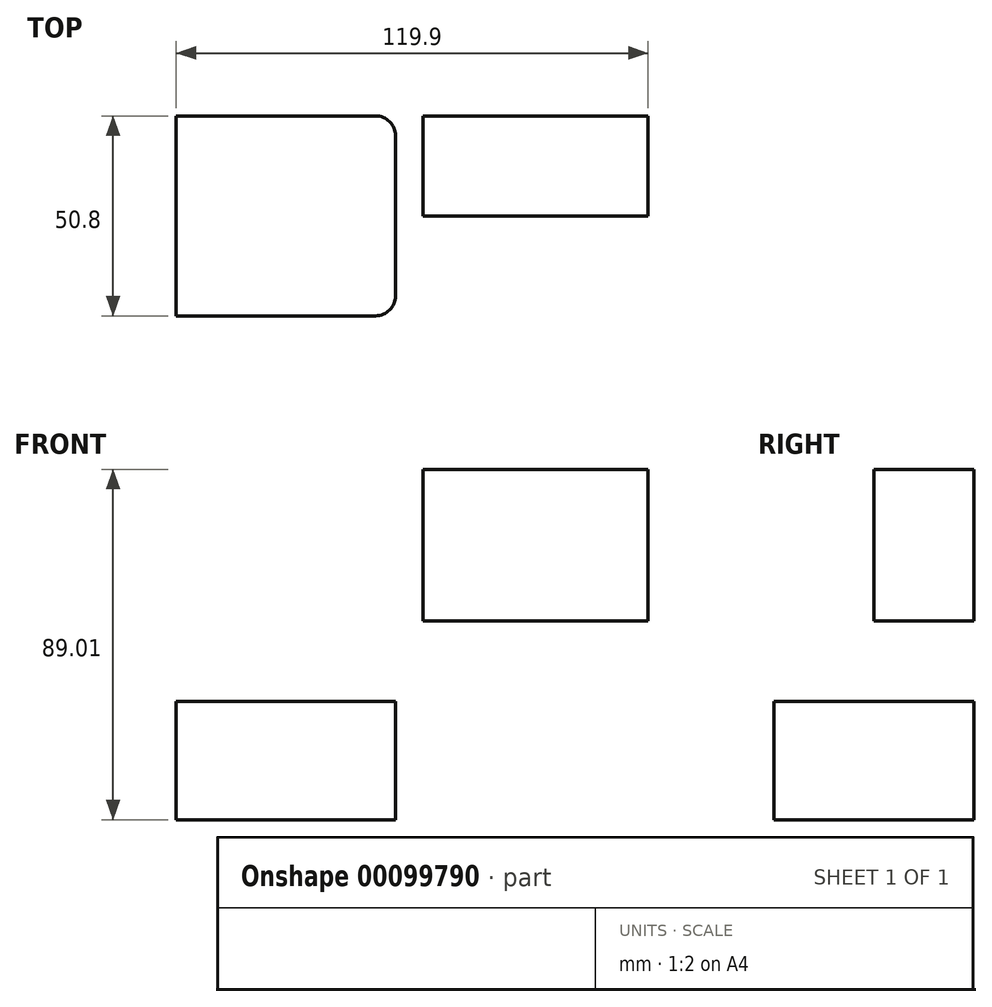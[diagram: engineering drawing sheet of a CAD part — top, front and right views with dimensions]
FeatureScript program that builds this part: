
annotation { "Feature Type Name" : "Feature", "Feature Type Description" : "" }
export const myFeature = defineFeature(function(context is Context, id is Id, definition is map)
    precondition{}
    {
        {
            var Q0;
            Q0=qCreatedBy(makeId("Front.planeOp"),FACE);
            var sketch = newSketch(context, id + "F0", { "sketchPlane" : qUnion([Q0])});
            skLineSegment(sketch, "E0.bottom", {"start": v(46.63, 19.3) * mm, "end": v(-46.63, 19.3) * mm});
            skLineSegment(sketch, "E0.top", {"start": v(46.63, -19.3) * mm, "end": v(-46.63, -19.3) * mm});
            skLineSegment(sketch, "E0.left", {"start": v(46.63, 19.3) * mm, "end": v(46.63, -19.3) * mm});
            skLineSegment(sketch, "E0.right", {"start": v(-46.63, 19.3) * mm, "end": v(-46.63, -19.3) * mm});
            skPoint(sketch, "E0.middle", {"position": v(0, 0) * mm});
            skLineSegment(sketch, "E1.bottom", {"start": v(110.8, 39.7) * mm, "end": v(53.63, 39.7) * mm});
            skLineSegment(sketch, "E1.top", {"start": v(110.8, 78.21) * mm, "end": v(53.63, 78.21) * mm});
            skLineSegment(sketch, "E1.left", {"start": v(110.8, 39.7) * mm, "end": v(110.8, 78.21) * mm});
            skLineSegment(sketch, "E1.right", {"start": v(53.63, 39.7) * mm, "end": v(53.63, 78.21) * mm});
            skPoint(sketch, "E1.middle", {"position": v(82.22, 58.96) * mm});
            skLineSegment(sketch, "E2", {"start": v(46.63, 19.3) * mm, "end": v(46.63, 45.25) * mm});
            skArc(sketch, "E3", {"start": v(46.63, 45.25) * mm, "mid": v(50.53, 53.16) * mm, "end": v(59.17, 54.88) * mm});
            skLineSegment(sketch, "E4.bottom", {"start": v(-9.1, -10.8) * mm, "end": v(50.8, -10.8) * mm});
            skLineSegment(sketch, "E4.top", {"start": v(-9.1, 41.27) * mm, "end": v(50.8, 41.27) * mm});
            skLineSegment(sketch, "E4.left", {"start": v(-9.1, -10.8) * mm, "end": v(-9.1, 41.27) * mm});
            skLineSegment(sketch, "E4.right", {"start": v(50.8, -10.8) * mm, "end": v(50.8, 41.27) * mm});
            skPoint(sketch, "E4.middle", {"position": v(20.84, 15.23) * mm});
            skSolve(sketch);
        }
        {
            var Q0;
            {var subQ0=sQuery(id+"F0.wireOp",EDGE,"E1.bottom");Q0=makeQuery(id+"F0.imprint","IMPRINT",FACE,{"disambiguationData":[TD([[makeQuery(id+"F0.imprint","IMPRINT",EDGE,{"derivedFrom":subQ0}),-1.0]])]});}
            var Q1;
            Q1=makeQuery(id+"F0.imprint","IMPRINT",FACE,{"disambiguationData":[TD([[makeQuery(id+"F0.imprint","IMPRINT",EDGE,{"derivedFrom":sQuery(id+"F0.wireOp",EDGE,"E0.bottom")}),1.0]])]});
            extrude(context, id + "F1", {"entities" : qUnion([Q0, Q1]), "depth" : 25.4 * mm});
        }
        {
            var Q0;
            Q0=makeQuery(id+"F1.opExtrude","CAP_FACE",FACE,{"disambiguationData":[OSD([sQuery(id+"F0.wireOp",EDGE,"E0.bottom"),sQuery(id+"F0.wireOp",EDGE,"E0.top"),sQuery(id+"F0.wireOp",EDGE,"E0.left"),sQuery(id+"F0.wireOp",EDGE,"E0.right")])],"isStart":false});
            extrude(context, id + "F2", {"entities" : qUnion([Q0]), "operationType" : NewBodyOperationType.ADD, "depth" : 25.4 * mm});
        }
        {
            var Q0;
            Q0=makeQuery(id+"F2.opExtrude","CAP_EDGE",EDGE,{"disambiguationData":[OSD([sQuery(id+"F0.wireOp",EDGE,"E0.left")])],"isStart":false});
            var Q1;
            Q1=makeQuery(id+"F2.opExtrude","CAP_EDGE",EDGE,{"disambiguationData":[OSD([sQuery(id+"F0.wireOp",EDGE,"E0.right")])],"isStart":false});
            var Q2;
            Q2=makeQuery(id+"F1.opExtrude","CAP_EDGE",EDGE,{"disambiguationData":[OSD([sQuery(id+"F0.wireOp",EDGE,"E0.left")])],"isStart":true});
            var Q3;
            Q3=makeQuery(id+"F1.opExtrude","CAP_EDGE",EDGE,{"disambiguationData":[OSD([sQuery(id+"F0.wireOp",EDGE,"E0.right")])],"isStart":true});
            fillet(context, id + "F3", {"entities" : qUnion([Q0, Q1, Q2, Q3]), "radius" : 5.08 * mm, "tangentPropagation" : true, "allowEdgeOverflow" : false});
        }
    });
